# Revit family: GMV-ND28-80TSB-T
name_source: partatom
category: 机械设备
revit_build: Autodesk Revit 2014 (Build: 20130308_1515(x64)
units: mm (PartAtom-declared; Revit-internal decimal feet)

## types (8) — shared parameters
drain pipe = 25  [stored 0.082021 ft]
main body depth = 630
main body height = 280
main body width = 790
panel depth = 710
panel thickness = 28
panel width = 1100

## per-type parameters (varying)
| type | cooling capacity | gas pipe | heating capacity | liquid pipe |
| GMV-ND28TS/B-T | 2800 W | 10  [stored 0.0328084 ft] | 3200 W | 6 |
| GMV-ND36TS/B-T | 3600 W | 10  [stored 0.0328084 ft] | 4000 W | 6 |
| GMV-ND45TS/B-T | 4500 W | 10  [stored 0.0328084 ft] | 5000 W | 6 |
| GMV-ND50TS/B-T | 5000 W | 10  [stored 0.0328084 ft] | 5600 W | 6 |
| GMV-ND56TS/B-T | 5600 W | 16 | 6300 W | 10  [stored 0.0328084 ft] |
| GMV-ND63TS/B-T | 6300 W | 16 | 7100 W | 10  [stored 0.0328084 ft] |
| GMV-ND71TS/B-T | 7100 W | 16 | 8000 W | 10  [stored 0.0328084 ft] |
| GMV-ND80TS/B-T | 8000 W | 16 | 9000 W | 10  [stored 0.0328084 ft] |

note: [stored X ft] marks values corroborated as IEEE doubles in the binary element streams (Revit-internal decimal feet)
